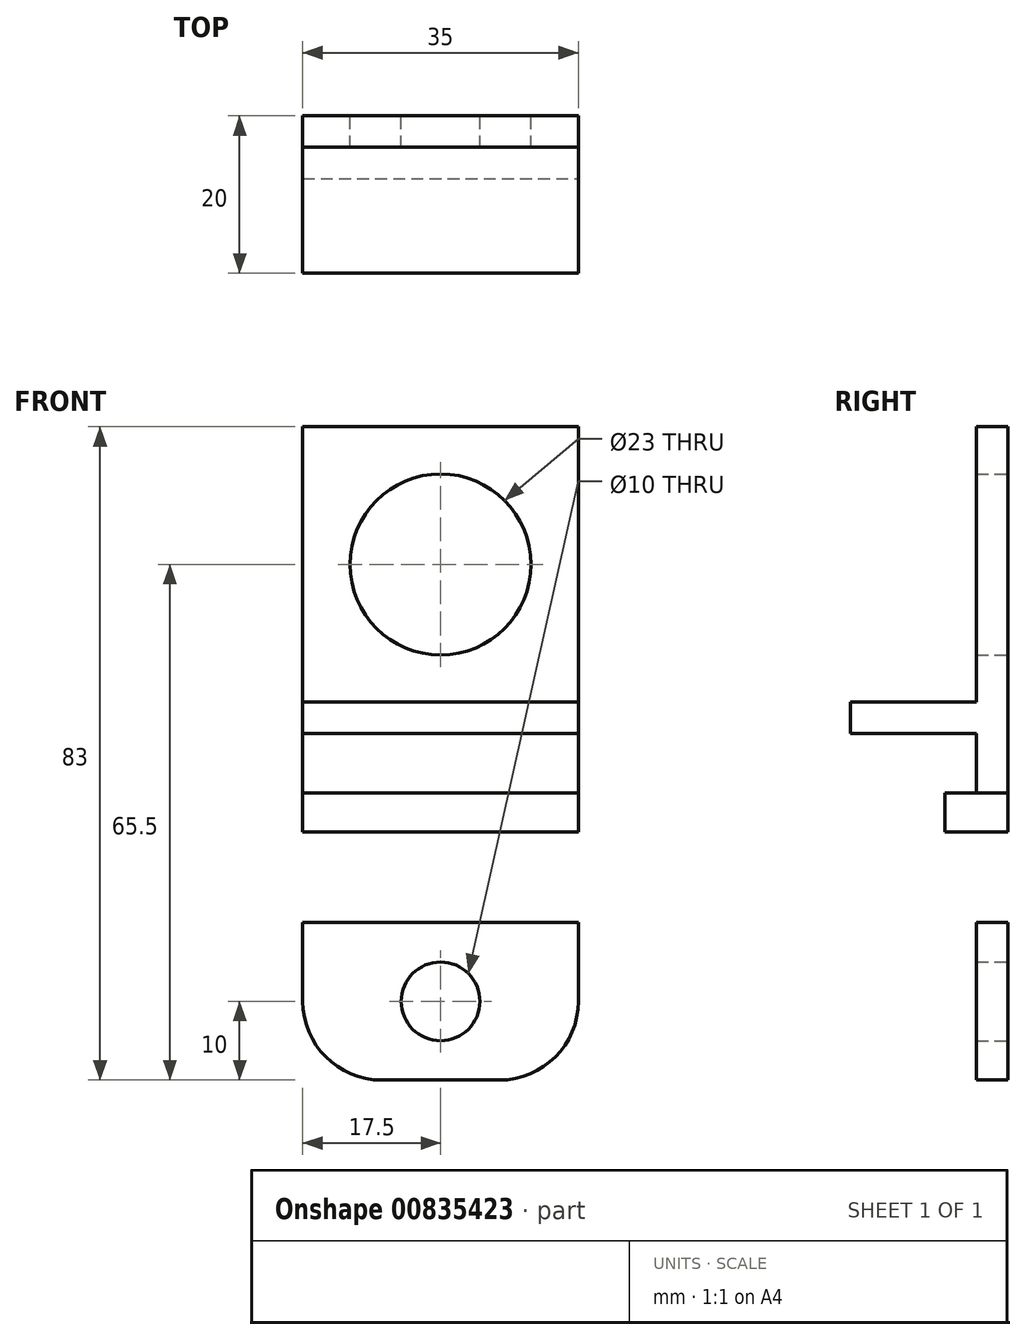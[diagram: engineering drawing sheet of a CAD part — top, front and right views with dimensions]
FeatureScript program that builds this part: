
annotation { "Feature Type Name" : "Feature", "Feature Type Description" : "" }
export const myFeature = defineFeature(function(context is Context, id is Id, definition is map)
    precondition{}
    {
        {
            var Q0;
            Q0=qCreatedBy(makeId("Front.planeOp"),FACE);
            var sketch = newSketch(context, id + "F0", { "sketchPlane" : qUnion([Q0])});
            skLineSegment(sketch, "E0.bottom", {"start": v(0, 0) * mm, "end": v(122.5, 0) * mm});
            skLineSegment(sketch, "E0.top", {"start": v(0, -4) * mm, "end": v(122.5, -4) * mm});
            skLineSegment(sketch, "E0.left", {"start": v(0, 0) * mm, "end": v(0, -4) * mm});
            skLineSegment(sketch, "E0.right", {"start": v(122.5, 0) * mm, "end": v(122.5, -4) * mm});
            skLineSegment(sketch, "E1.top", {"start": v(0, -24) * mm, "end": v(122.5, -24) * mm});
            skLineSegment(sketch, "E1.left", {"start": v(0, -4) * mm, "end": v(0, -24) * mm});
            skLineSegment(sketch, "E1.right", {"start": v(122.5, -4) * mm, "end": v(122.5, -24) * mm});
            skLineSegment(sketch, "E2", {"start": v(0, 0) * mm, "end": v(0, 132.5) * mm});
            skLineSegment(sketch, "E3", {"start": v(0, 132.5) * mm, "end": v(22.5, 132.5) * mm});
            skCircle(sketch, "E4", {"center": v(22.5, 132.5) * mm, "radius": 3.98 * mm});
            skCircle(sketch, "E5", {"center": v(22.5, 132.5) * mm, "radius": 11 * mm});
            skCircle(sketch, "E6", {"center": v(22.5, 132.5) * mm, "radius": 22.5 * mm});
            skLineSegment(sketch, "E7", {"start": v(38.4, 148.4) * mm, "end": v(122.5, 64.32) * mm});
            skLineSegment(sketch, "E8", {"start": v(122.5, 0) * mm, "end": v(122.5, 64.32) * mm});
            skCircle(sketch, "E9", {"center": v(105, 17.5) * mm, "radius": 11.5 * mm});
            skLineSegment(sketch, "E10", {"start": v(0, -11.5) * mm, "end": v(122.5, -11.5) * mm});
            skLineSegment(sketch, "E11", {"start": v(0, -16.5) * mm, "end": v(122.5, -16.5) * mm});
            skLineSegment(sketch, "E12", {"start": v(87.5, -24) * mm, "end": v(87.5, 35) * mm});
            skLineSegment(sketch, "E13", {"start": v(87.5, 35) * mm, "end": v(122.5, 35) * mm});
            skPoint(sketch, "E14", {"position": v(105, 35) * mm});
            skPoint(sketch, "E15", {"position": v(87.5, 0) * mm});
            skPoint(sketch, "E16", {"position": v(87.5, 17.5) * mm});
            skLineSegment(sketch, "E17.bottom", {"start": v(87.5, -24) * mm, "end": v(122.5, -24) * mm});
            skLineSegment(sketch, "E17.top", {"start": v(87.5, -28) * mm, "end": v(122.5, -28) * mm});
            skLineSegment(sketch, "E17.left", {"start": v(87.5, -24) * mm, "end": v(87.5, -28) * mm});
            skLineSegment(sketch, "E17.right", {"start": v(122.5, -24) * mm, "end": v(122.5, -28) * mm});
            skLineSegment(sketch, "E18.top", {"start": v(97.5, -48) * mm, "end": v(112.5, -48) * mm});
            skLineSegment(sketch, "E18.left", {"start": v(87.5, -28) * mm, "end": v(87.5, -38) * mm});
            skLineSegment(sketch, "E18.right", {"start": v(122.5, -28) * mm, "end": v(122.5, -38) * mm});
            skPoint(sketch, "E19", {"position": v(87.5, -38) * mm});
            skPoint(sketch, "E20", {"position": v(105, -48) * mm});
            skCircle(sketch, "E21", {"center": v(105, -38) * mm, "radius": 5 * mm});
            skPoint(sketch, "E22.visualSharp", {"position": v(87.5, -48) * mm});
            skArc(sketch, "E22.filletArc", {"start": v(87.5, -38) * mm, "mid": v(90.43, -45.07) * mm, "end": v(97.5, -48) * mm});
            skPoint(sketch, "E23.visualSharp", {"position": v(122.5, -48) * mm});
            skArc(sketch, "E23.filletArc", {"start": v(112.5, -48) * mm, "mid": v(119.57, -45.07) * mm, "end": v(122.5, -38) * mm});
            skSolve(sketch);
        }
        {
            var Q0;
            Q0=makeQuery(id+"F0.imprint","IMPRINT",FACE,{"disambiguationData":[TD([[makeQuery(id+"F0.imprint","IMPRINT",EDGE,{"derivedFrom":sQuery(id+"F0.wireOp",EDGE,"E9")}),-1.0]])]});
            var Q1;
            {var subQ0=sQuery(id+"F0.wireOp",EDGE,"E1.right");var subQ5=sQuery(id+"F0.wireOp",EDGE,"E10");var subQ6=makeQuery(id+"F0.imprint","INTERSECT",VERTEX,{"derivedFrom":[subQ0,subQ5]});Q1=makeQuery(id+"F0.imprint","IMPRINT",FACE,{"disambiguationData":[TD([[makeQuery(id+"F0.imprint","IMPRINT",EDGE,{"disambiguationData":[TD([[subQ6,1.0]])],"derivedFrom":subQ5}),1.0]])]});}
            var Q2;
            {var subQ0=sQuery(id+"F0.wireOp",EDGE,"E17.bottom");Q2=makeQuery(id+"F0.imprint","IMPRINT",FACE,{"disambiguationData":[TD([[makeQuery(id+"F0.imprint","IMPRINT",EDGE,{"derivedFrom":subQ0}),1.0]])]});}
            var Q3;
            Q3=makeQuery(id+"F0.imprint","IMPRINT",FACE,{"disambiguationData":[TD([[makeQuery(id+"F0.imprint","IMPRINT",EDGE,{"derivedFrom":sQuery(id+"F0.wireOp",EDGE,"E17.top")}),-1.0]])]});
            extrude(context, id + "F1", {"entities" : qUnion([Q0, Q1, Q2, Q3]), "depth" : 4 * mm, "offsetDistance" : 25 * mm});
        }
        {
            var Q0;
            {var subQ0=sQuery(id+"F0.wireOp",EDGE,"E0.right");Q0=makeQuery(id+"F0.imprint","IMPRINT",FACE,{"disambiguationData":[TD([[makeQuery(id+"F0.imprint","IMPRINT",EDGE,{"derivedFrom":subQ0}),-1.0]])]});}
            var Q1;
            Q1=makeQuery(id+"F0.imprint","IMPRINT",FACE,{"disambiguationData":[TD([[makeQuery(id+"F0.imprint","IMPRINT",EDGE,{"derivedFrom":sQuery(id+"F0.wireOp",EDGE,"E17.bottom")}),-1.0]])]});
            extrude(context, id + "F2", {"entities" : qUnion([Q0, Q1]), "operationType" : NewBodyOperationType.ADD, "depth" : 20 * mm, "offsetDistance" : 25 * mm});
        }
        {
            var Q0;
            {var subQ0=sQuery(id+"F0.wireOp",EDGE,"E10");var subQ1=sQuery(id+"F0.wireOp",EDGE,"E1.right");var subQ2=makeQuery(id+"F0.imprint","INTERSECT",VERTEX,{"derivedFrom":[subQ1,subQ0]});Q0=makeQuery(id+"F0.imprint","IMPRINT",FACE,{"disambiguationData":[TD([[makeQuery(id+"F0.imprint","IMPRINT",EDGE,{"disambiguationData":[TD([[subQ2,-1.0]])],"derivedFrom":subQ1}),-1.0]])]});}
            extrude(context, id + "F3", {"entities" : qUnion([Q0]), "depth" : 8 * mm, "offsetDistance" : 25 * mm});
        }
    });
